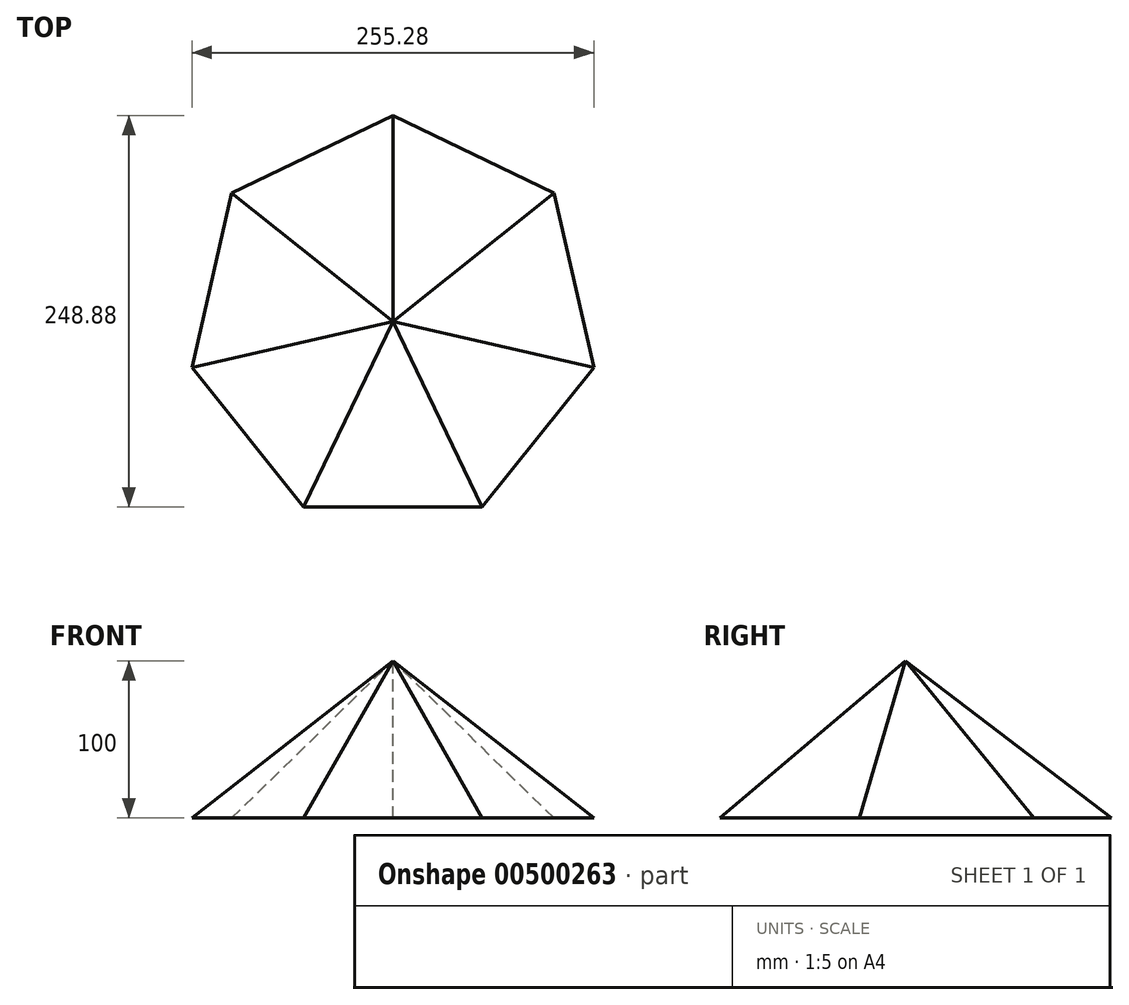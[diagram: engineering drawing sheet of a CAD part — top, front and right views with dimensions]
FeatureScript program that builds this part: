
annotation { "Feature Type Name" : "Feature", "Feature Type Description" : "" }
export const myFeature = defineFeature(function(context is Context, id is Id, definition is map)
    precondition{}
    {
        {
            var Q0;
            Q0=qCreatedBy(makeId("Top.planeOp"),FACE);
            var sketch = newSketch(context, id + "F0", { "sketchPlane" : qUnion([Q0])});
            skCircle(sketch, "E0.cCircle", {"center": v(0, 0) * mm, "radius": 130.92 * mm, "construction": true});
            skLineSegment(sketch, "E0.0", {"start": v(56.8, -117.96) * mm, "end": v(-56.8, -117.96) * mm});
            skLineSegment(sketch, "E0.1", {"start": v(-56.8, -117.96) * mm, "end": v(-127.64, -29.13) * mm});
            skLineSegment(sketch, "E0.2", {"start": v(-127.64, -29.13) * mm, "end": v(-102.36, 81.63) * mm});
            skLineSegment(sketch, "E0.3", {"start": v(-102.36, 81.63) * mm, "end": v(0, 130.92) * mm});
            skLineSegment(sketch, "E0.4", {"start": v(0, 130.92) * mm, "end": v(102.36, 81.63) * mm});
            skLineSegment(sketch, "E0.5", {"start": v(102.36, 81.63) * mm, "end": v(127.64, -29.13) * mm});
            skLineSegment(sketch, "E0.6", {"start": v(127.64, -29.13) * mm, "end": v(56.8, -117.96) * mm});
            skSolve(sketch);
        }
        {
            var Q0;
            Q0=qCreatedBy(makeId("Top.planeOp"),FACE);
            cPlane(context, id + "F1", {"entities" : qUnion([Q0]), "cplaneType" : CPlaneType.OFFSET, "offset" : 100 * mm, "width" : 150 * mm, "height" : 150 * mm});
        }
        {
            var Q0;
            Q0=qCreatedBy(id+"F1.planeOp",FACE);
            var sketch = newSketch(context, id + "F2", { "sketchPlane" : qUnion([Q0])});
            skPoint(sketch, "E1", {"position": v(0, 0) * mm});
            skSolve(sketch);
        }
        {
            var Q0;
            Q0=makeQuery(id+"F0.imprint","IMPRINT",FACE,{"disambiguationData":[TD([[makeQuery(id+"F0.imprint","IMPRINT",EDGE,{"derivedFrom":sQuery(id+"F0.wireOp",EDGE,"E0.0")}),-1.0]])]});
            var Q1;
            Q1=sQuery(id+"F2.wireOp",VERTEX,"E1");
            loft(context, id + "F3", {"sheetProfilesArray" : [{ "sheetProfileEntities" : qUnion([Q0]) }, { "sheetProfileEntities" : qUnion([Q1]) }]});
        }
    });
